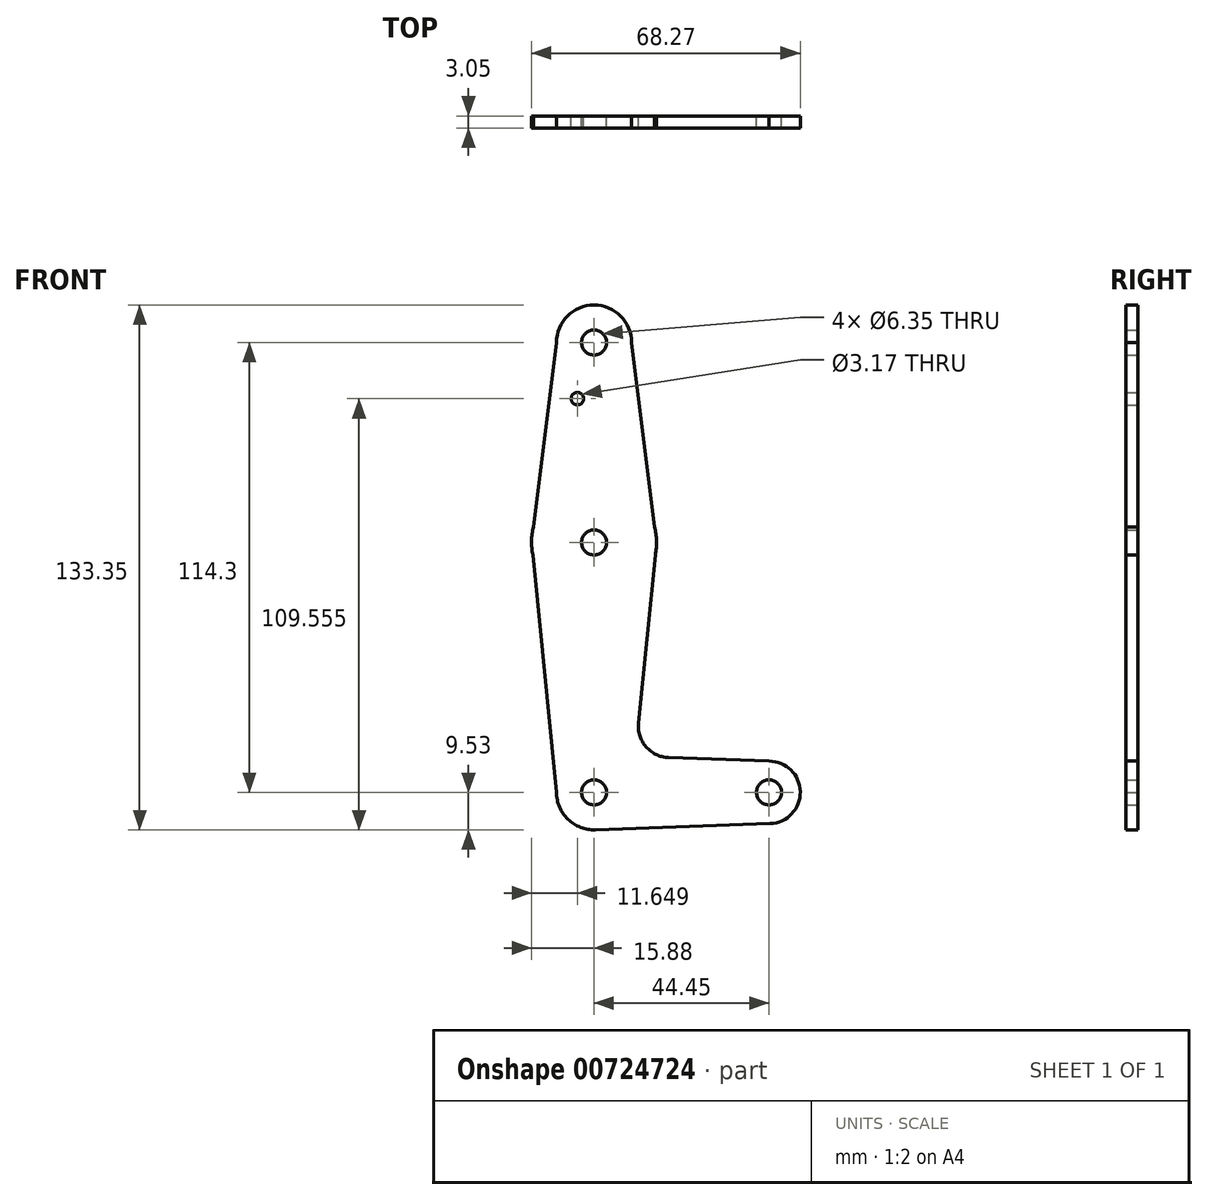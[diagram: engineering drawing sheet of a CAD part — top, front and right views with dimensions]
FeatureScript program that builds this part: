
annotation { "Feature Type Name" : "Feature", "Feature Type Description" : "" }
export const myFeature = defineFeature(function(context is Context, id is Id, definition is map)
    precondition{}
    {
        {
            var Q0;
            Q0=qCreatedBy(makeId("Front.planeOp"),FACE);
            var sketch = newSketch(context, id + "F0", { "sketchPlane" : qUnion([Q0])});
            skLineSegment(sketch, "E0", {"start": v(0, 0) * mm, "end": v(0, -63.5) * mm});
            skLineSegment(sketch, "E1", {"start": v(0, -63.5) * mm, "end": v(0, 50.8) * mm, "construction": true});
            skCircle(sketch, "E2", {"center": v(0, 0) * mm, "radius": 15.88 * mm});
            skCircle(sketch, "E3", {"center": v(0, 50.8) * mm, "radius": 9.53 * mm});
            skLineSegment(sketch, "E4", {"start": v(0, -63.5) * mm, "end": v(44.45, -63.5) * mm, "construction": true});
            skCircle(sketch, "E5", {"center": v(0, -63.5) * mm, "radius": 9.53 * mm});
            skCircle(sketch, "E6", {"center": v(44.45, -63.5) * mm, "radius": 7.94 * mm});
            skLineSegment(sketch, "E7", {"start": v(15.88, 0) * mm, "end": v(9.52, 50.8) * mm});
            skLineSegment(sketch, "E8", {"start": v(15.88, 0) * mm, "end": v(11.28, -45.91) * mm});
            skLineSegment(sketch, "E9", {"start": v(-9.52, 50.8) * mm, "end": v(-15.88, 0) * mm});
            skLineSegment(sketch, "E10", {"start": v(-9.52, -63.5) * mm, "end": v(-15.88, 0) * mm});
            skLineSegment(sketch, "E11", {"start": v(0.34, -73.02) * mm, "end": v(44.73, -71.43) * mm});
            skLineSegment(sketch, "E12", {"start": v(44.45, -55.56) * mm, "end": v(18.9, -54.65) * mm});
            skLineSegment(sketch, "E13", {"start": v(0, 0) * mm, "end": v(0, 36.53) * mm});
            skCircle(sketch, "E14", {"center": v(-4.23, 36.53) * mm, "radius": 1.59 * mm});
            skPoint(sketch, "E15.newPointB", {"position": v(0, -53.97) * mm});
            skArc(sketch, "E15.filletArc", {"start": v(11.28, -45.91) * mm, "mid": v(13.2, -51.93) * mm, "end": v(18.9, -54.65) * mm});
            skCircle(sketch, "E16", {"center": v(44.45, -63.5) * mm, "radius": 3.18 * mm});
            skCircle(sketch, "E17", {"center": v(0, -63.5) * mm, "radius": 3.18 * mm});
            skCircle(sketch, "E18", {"center": v(0, 0) * mm, "radius": 3.17 * mm});
            skCircle(sketch, "E19", {"center": v(0, 50.8) * mm, "radius": 3.18 * mm});
            skSolve(sketch);
        }
        {
            var Q0;
            Q0 = qSketchRegion(id + "F0", true);
            extrude(context, id + "F1", {"entities" : qUnion([Q0]), "depth" : 3.05 * mm, "offsetDistance" : 25.4 * mm});
        }
    });
